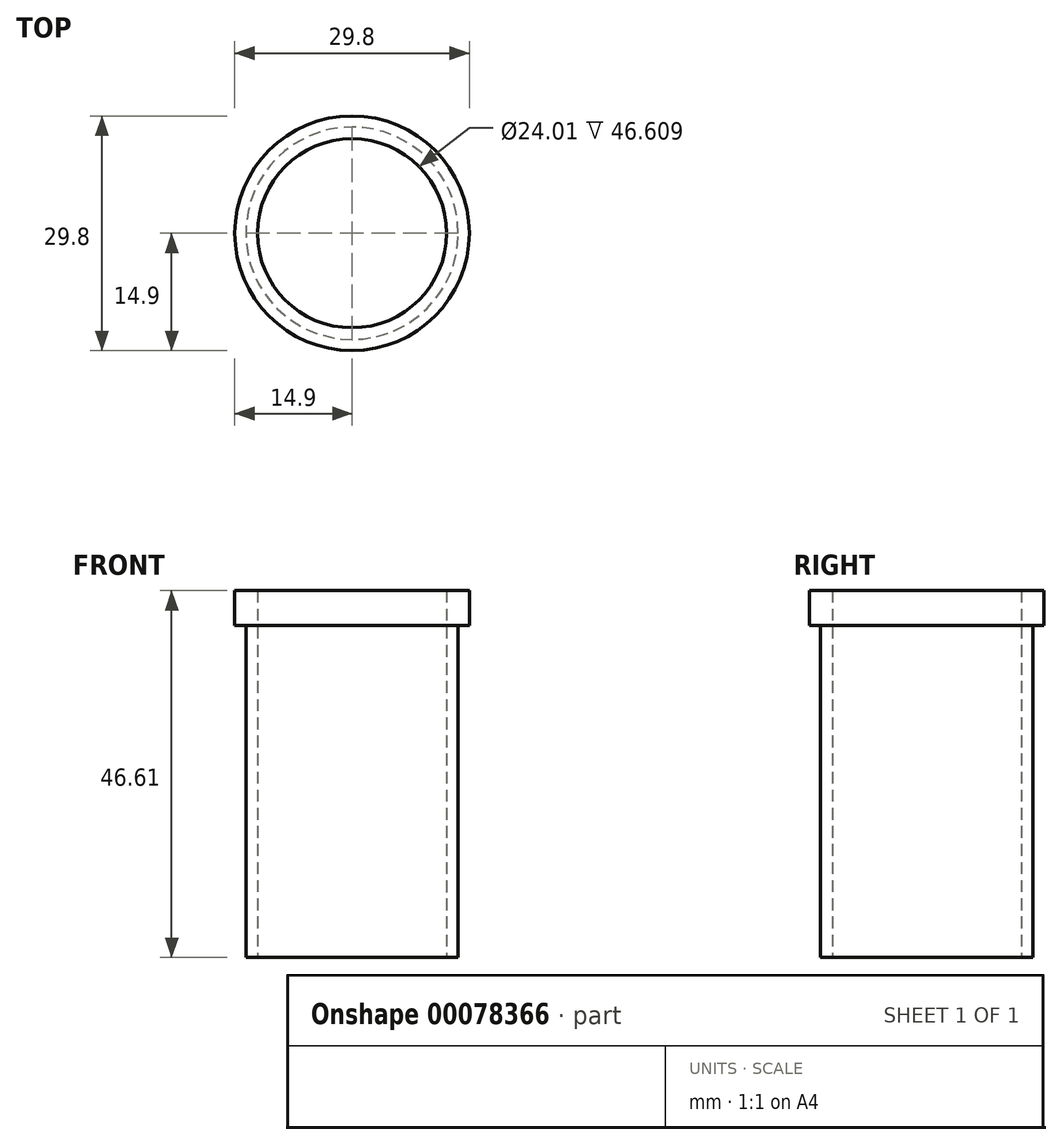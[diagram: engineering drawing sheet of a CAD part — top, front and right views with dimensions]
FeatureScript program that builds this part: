
annotation { "Feature Type Name" : "Feature", "Feature Type Description" : "" }
export const myFeature = defineFeature(function(context is Context, id is Id, definition is map)
    precondition{}
    {
        {
            var Q0;
            Q0=qCreatedBy(makeId("Top.planeOp"),FACE);
            var sketch = newSketch(context, id + "F0", { "sketchPlane" : qUnion([Q0])});
            skCircle(sketch, "E0", {"center": v(0, 0) * mm, "radius": 13.5 * mm});
            skCircle(sketch, "E1", {"center": v(0, 0) * mm, "radius": 12 * mm});
            skSolve(sketch);
        }
        {
            var Q0;
            Q0 = qSketchRegion(id + "F0", true);
            extrude(context, id + "F1", {"entities" : qUnion([Q0]), "depth" : 46.6 * mm});
        }
        {
            var Q0;
            Q0=makeQuery(id+"F1.opExtrude","CAP_FACE",FACE,{"disambiguationData":[OSD([sQuery(id+"F0.wireOp",EDGE,"E0"),sQuery(id+"F0.wireOp",EDGE,"E1")])],"isStart":false});
            var sketch = newSketch(context, id + "F2", { "sketchPlane" : qUnion([Q0])});
            skCircle(sketch, "E2", {"center": v(0, 0) * mm, "radius": 12 * mm});
            skCircle(sketch, "E3", {"center": v(0, 0) * mm, "radius": 14.9 * mm});
            skSolve(sketch);
        }
        {
            var Q0;
            Q0 = qSketchRegion(id + "F2", true);
            extrude(context, id + "F3", {"entities" : qUnion([Q0]), "operationType" : NewBodyOperationType.ADD, "oppositeDirection" : true, "depth" : 4.44 * mm});
        }
    });
